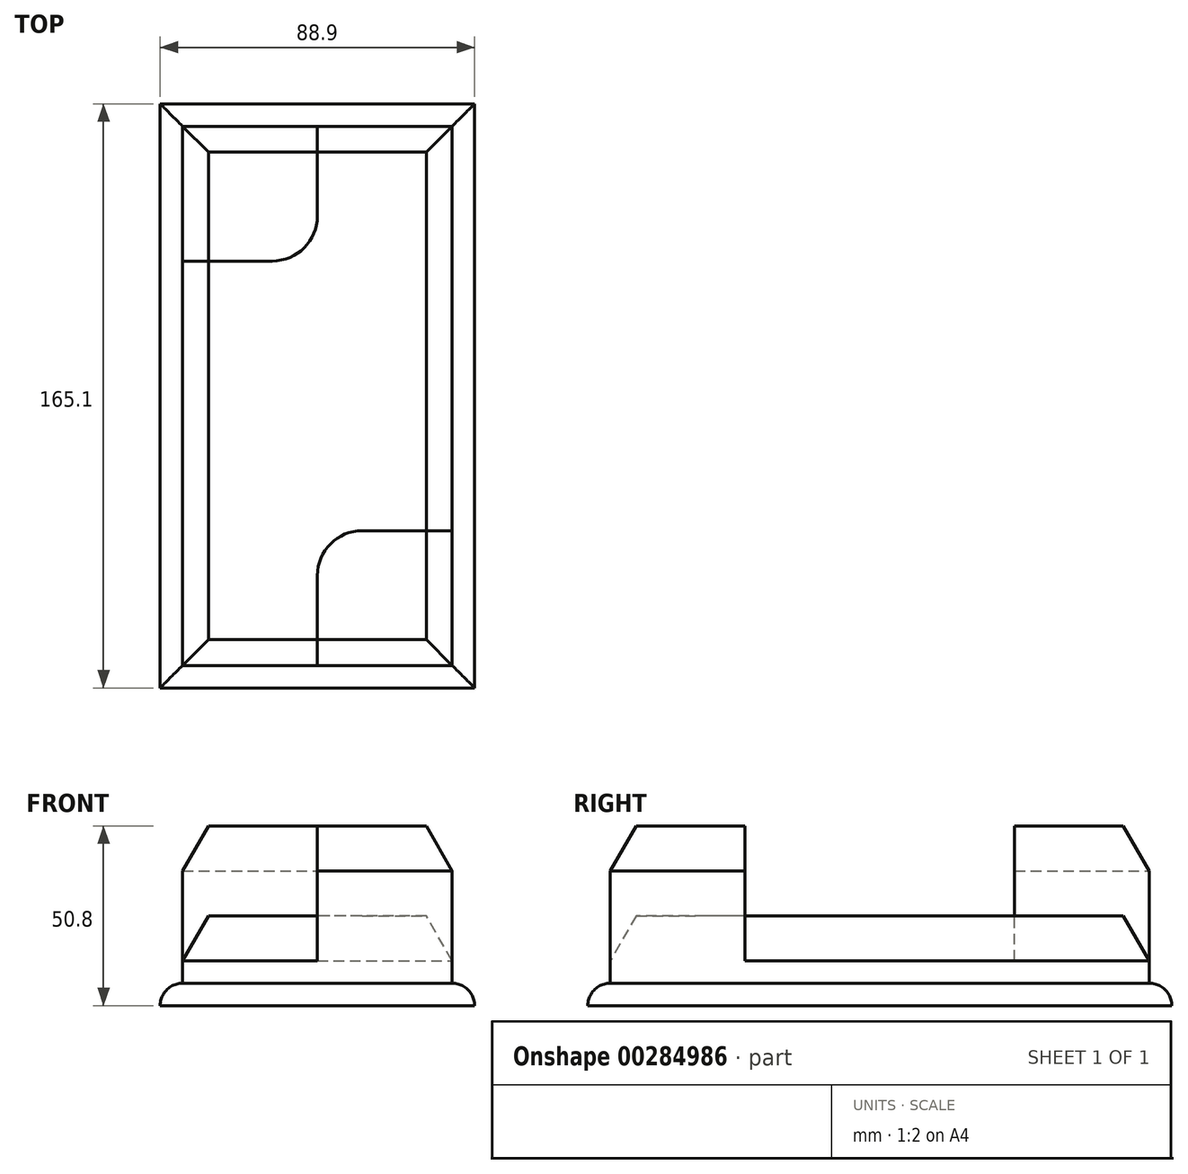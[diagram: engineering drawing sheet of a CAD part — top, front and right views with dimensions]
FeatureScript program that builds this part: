
annotation { "Feature Type Name" : "Feature", "Feature Type Description" : "" }
export const myFeature = defineFeature(function(context is Context, id is Id, definition is map)
    precondition{}
    {
        {
            var Q0;
            Q0=qCreatedBy(makeId("Top.planeOp"),FACE);
            var sketch = newSketch(context, id + "F0", { "sketchPlane" : qUnion([Q0])});
            skLineSegment(sketch, "E0", {"start": v(-38.1, 0) * mm, "end": v(-38.1, -152.4) * mm});
            skLineSegment(sketch, "E1", {"start": v(-38.1, -152.4) * mm, "end": v(38.1, -152.4) * mm});
            skLineSegment(sketch, "E2", {"start": v(38.1, -152.4) * mm, "end": v(38.1, 0) * mm});
            skLineSegment(sketch, "E3", {"start": v(38.1, 0) * mm, "end": v(-38.1, 0) * mm});
            skLineSegment(sketch, "E4.0", {"start": v(44.45, -158.75) * mm, "end": v(44.45, 6.35) * mm});
            skLineSegment(sketch, "E4.1", {"start": v(-44.45, -158.75) * mm, "end": v(44.45, -158.75) * mm});
            skLineSegment(sketch, "E4.2", {"start": v(-44.45, 6.35) * mm, "end": v(-44.45, -158.75) * mm});
            skLineSegment(sketch, "E4.3", {"start": v(44.45, 6.35) * mm, "end": v(-44.45, 6.35) * mm});
            skLineSegment(sketch, "E5", {"start": v(0, 0) * mm, "end": v(0, -25.4) * mm});
            skLineSegment(sketch, "E6", {"start": v(-12.7, -38.1) * mm, "end": v(-38.1, -38.1) * mm});
            skLineSegment(sketch, "E7", {"start": v(0, -152.4) * mm, "end": v(0, -127) * mm});
            skLineSegment(sketch, "E8", {"start": v(12.7, -114.3) * mm, "end": v(38.1, -114.3) * mm});
            skPoint(sketch, "E9.visualSharp", {"position": v(0, -38.1) * mm});
            skArc(sketch, "E9.filletArc", {"start": v(-12.7, -38.1) * mm, "mid": v(-3.72, -34.38) * mm, "end": v(0, -25.4) * mm});
            skPoint(sketch, "E10.visualSharp", {"position": v(0, -114.3) * mm});
            skArc(sketch, "E10.filletArc", {"start": v(12.7, -114.3) * mm, "mid": v(3.72, -118.02) * mm, "end": v(0, -127) * mm});
            skSolve(sketch);
        }
        {
            var Q0;
            Q0 = qSketchRegion(id + "F0", true);
            var Q1;
            {var subQ9=sQuery(id+"F0.wireOp",EDGE,"E5");Q1=makeQuery(id+"F0.imprint","IMPRINT",FACE,{"disambiguationData":[TD([[makeQuery(id+"F0.imprint","IMPRINT",EDGE,{"derivedFrom":subQ9}),1.0]])]});}
            var Q2;
            {var subQ1=sQuery(id+"F0.wireOp",EDGE,"E5");Q2=makeQuery(id+"F0.imprint","IMPRINT",FACE,{"disambiguationData":[TD([[makeQuery(id+"F0.imprint","IMPRINT",EDGE,{"derivedFrom":subQ1}),-1.0]])]});}
            var Q3;
            {var subQ4=sQuery(id+"F0.wireOp",EDGE,"E7");Q3=makeQuery(id+"F0.imprint","IMPRINT",FACE,{"disambiguationData":[TD([[makeQuery(id+"F0.imprint","IMPRINT",EDGE,{"derivedFrom":subQ4}),-1.0]])]});}
            extrude(context, id + "F1", {"entities" : qUnion([Q0, Q1, Q2, Q3]), "depth" : 6.35 * mm});
        }
        {
            var Q0;
            {var subQ9=sQuery(id+"F0.wireOp",EDGE,"E5");Q0=makeQuery(id+"F0.imprint","IMPRINT",FACE,{"disambiguationData":[TD([[makeQuery(id+"F0.imprint","IMPRINT",EDGE,{"derivedFrom":subQ9}),1.0]])]});}
            extrude(context, id + "F2", {"entities" : qUnion([Q0]), "operationType" : NewBodyOperationType.ADD, "depth" : 25.4 * mm});
        }
        {
            var Q0;
            {var subQ4=sQuery(id+"F0.wireOp",EDGE,"E7");Q0=makeQuery(id+"F0.imprint","IMPRINT",FACE,{"disambiguationData":[TD([[makeQuery(id+"F0.imprint","IMPRINT",EDGE,{"derivedFrom":subQ4}),-1.0]])]});}
            var Q1;
            {var subQ1=sQuery(id+"F0.wireOp",EDGE,"E5");Q1=makeQuery(id+"F0.imprint","IMPRINT",FACE,{"disambiguationData":[TD([[makeQuery(id+"F0.imprint","IMPRINT",EDGE,{"derivedFrom":subQ1}),-1.0]])]});}
            extrude(context, id + "F3", {"entities" : qUnion([Q0, Q1]), "operationType" : NewBodyOperationType.ADD, "depth" : 50.8 * mm});
        }
        {
            var Q0;
            Q0=makeQuery(id+"F3.opExtrude","CAP_EDGE",EDGE,{"disambiguationData":[OSD([sQuery(id+"F0.wireOp",EDGE,"E2")])],"isStart":false});
            var Q1;
            Q1=makeQuery(id+"F3.opExtrude","CAP_EDGE",EDGE,{"disambiguationData":[OSD([sQuery(id+"F0.wireOp",EDGE,"E1")])],"isStart":false});
            var Q2;
            Q2=makeQuery(id+"F3.opExtrude","CAP_EDGE",EDGE,{"disambiguationData":[OSD([sQuery(id+"F0.wireOp",EDGE,"E3")])],"isStart":false});
            var Q3;
            Q3=makeQuery(id+"F3.opExtrude","CAP_EDGE",EDGE,{"disambiguationData":[OSD([sQuery(id+"F0.wireOp",EDGE,"E0")])],"isStart":false});
            var Q4;
            Q4=makeQuery(id+"F2.opExtrude","CAP_EDGE",EDGE,{"disambiguationData":[OSD([sQuery(id+"F0.wireOp",EDGE,"E0")])],"isStart":false});
            var Q5;
            Q5=makeQuery(id+"F2.opExtrude","CAP_EDGE",EDGE,{"disambiguationData":[OSD([sQuery(id+"F0.wireOp",EDGE,"E1")])],"isStart":false});
            var Q6;
            Q6=makeQuery(id+"F2.opExtrude","CAP_EDGE",EDGE,{"disambiguationData":[OSD([sQuery(id+"F0.wireOp",EDGE,"E2")])],"isStart":false});
            var Q7;
            Q7=makeQuery(id+"F2.opExtrude","CAP_EDGE",EDGE,{"disambiguationData":[OSD([sQuery(id+"F0.wireOp",EDGE,"E3")])],"isStart":false});
            chamfer(context, id + "F4", {"entities" : qUnion([Q0, Q1, Q2, Q3, Q4, Q5, Q6, Q7]), "chamferType" : ChamferType.OFFSET_ANGLE, "width" : 12.7 * mm, "oppositeDirection" : true, "angle" : 30 * degree, "tangentPropagation" : true});
        }
        {
            var Q0;
            Q0=makeQuery(id+"F1.opExtrude","CAP_EDGE",EDGE,{"disambiguationData":[OSD([sQuery(id+"F0.wireOp",EDGE,"E4.0")])],"isStart":false});
            var Q1;
            Q1=makeQuery(id+"F1.opExtrude","CAP_EDGE",EDGE,{"disambiguationData":[OSD([sQuery(id+"F0.wireOp",EDGE,"E4.3")])],"isStart":false});
            var Q2;
            Q2=makeQuery(id+"F1.opExtrude","CAP_EDGE",EDGE,{"disambiguationData":[OSD([sQuery(id+"F0.wireOp",EDGE,"E4.2")])],"isStart":false});
            var Q3;
            Q3=makeQuery(id+"F1.opExtrude","CAP_EDGE",EDGE,{"disambiguationData":[OSD([sQuery(id+"F0.wireOp",EDGE,"E4.1")])],"isStart":false});
            fillet(context, id + "F5", {"entities" : qUnion([Q0, Q1, Q2, Q3]), "radius" : 6.35 * mm, "tangentPropagation" : true, "allowEdgeOverflow" : false});
        }
    });
